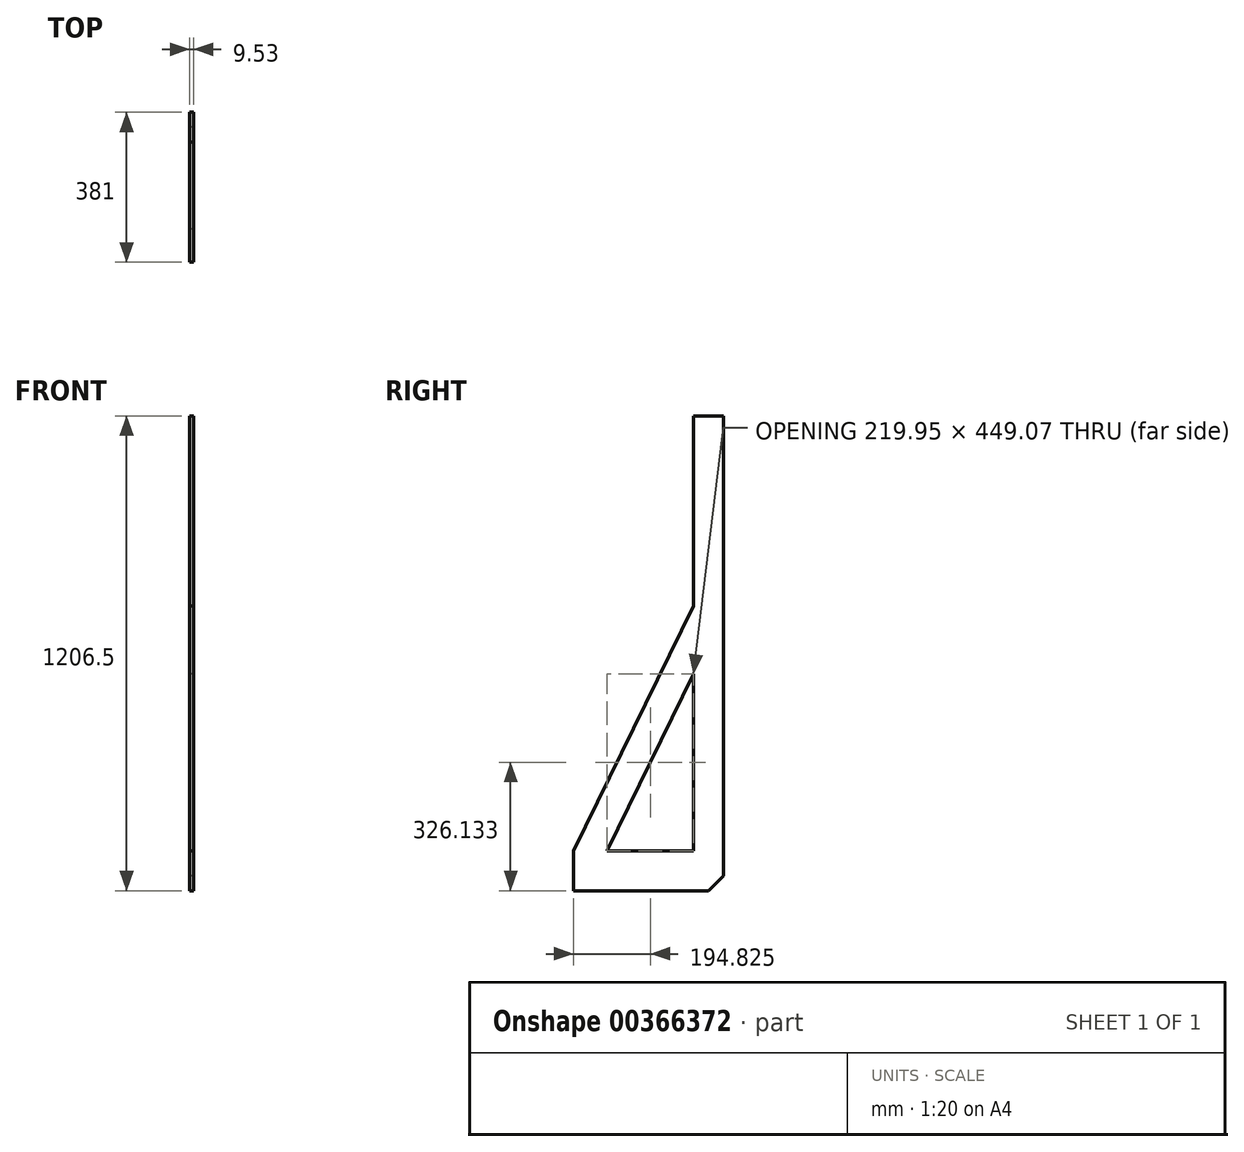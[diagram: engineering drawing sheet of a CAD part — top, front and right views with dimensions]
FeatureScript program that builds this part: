
annotation { "Feature Type Name" : "Feature", "Feature Type Description" : "" }
export const myFeature = defineFeature(function(context is Context, id is Id, definition is map)
    precondition{}
    {
        {
            var Q0;
            Q0=qCreatedBy(makeId("Right.planeOp"),FACE);
            var sketch = newSketch(context, id + "F0", { "sketchPlane" : qUnion([Q0])});
            skLineSegment(sketch, "E0.bottom", {"start": v(0, 0) * mm, "end": v(-381, 0) * mm});
            skLineSegment(sketch, "E0.top", {"start": v(0, 723.9) * mm, "end": v(-76.2, 723.9) * mm});
            skLineSegment(sketch, "E0.left", {"start": v(0, 0) * mm, "end": v(0, 723.9) * mm});
            skLineSegment(sketch, "E0.right", {"start": v(-381, 0) * mm, "end": v(-381, 101.6) * mm});
            skLineSegment(sketch, "E1.0", {"start": v(-76.2, 101.6) * mm, "end": v(-381, 101.6) * mm});
            skLineSegment(sketch, "E2.0", {"start": v(-76.2, 101.6) * mm, "end": v(-76.2, 723.9) * mm});
            skLineSegment(sketch, "E3", {"start": v(-381, 101.6) * mm, "end": v(-76.2, 723.9) * mm});
            skLineSegment(sketch, "E4.0", {"start": v(-296.15, 101.6) * mm, "end": v(-76.2, 550.67) * mm});
            skLineSegment(sketch, "E5", {"start": v(0, 38.1) * mm, "end": v(-38.1, 0) * mm});
            skLineSegment(sketch, "E6.top", {"start": v(0, 1206.5) * mm, "end": v(-76.2, 1206.5) * mm});
            skLineSegment(sketch, "E6.left", {"start": v(0, 723.9) * mm, "end": v(0, 1206.5) * mm});
            skLineSegment(sketch, "E6.right", {"start": v(-76.2, 723.9) * mm, "end": v(-76.2, 1206.5) * mm});
            skSolve(sketch);
        }
        {
            var Q0;
            Q0=makeQuery(id+"F0.imprint","IMPRINT",FACE,{"disambiguationData":[TD([[makeQuery(id+"F0.imprint","IMPRINT",EDGE,{"derivedFrom":sQuery(id+"F0.wireOp",EDGE,"E0.top")}),-1.0]])]});
            var Q1;
            {var subQ5=sQuery(id+"F0.wireOp",EDGE,"E0.right");Q1=makeQuery(id+"F0.imprint","IMPRINT",FACE,{"disambiguationData":[TD([[makeQuery(id+"F0.imprint","IMPRINT",EDGE,{"derivedFrom":subQ5}),-1.0]])]});}
            var Q2;
            {var subQ0=sQuery(id+"F0.wireOp",EDGE,"E3");Q2=makeQuery(id+"F0.imprint","IMPRINT",FACE,{"disambiguationData":[TD([[makeQuery(id+"F0.imprint","IMPRINT",EDGE,{"derivedFrom":subQ0}),-1.0]])]});}
            extrude(context, id + "F1", {"entities" : qUnion([Q0, Q1, Q2]), "depth" : 9.52 * mm});
        }
    });
